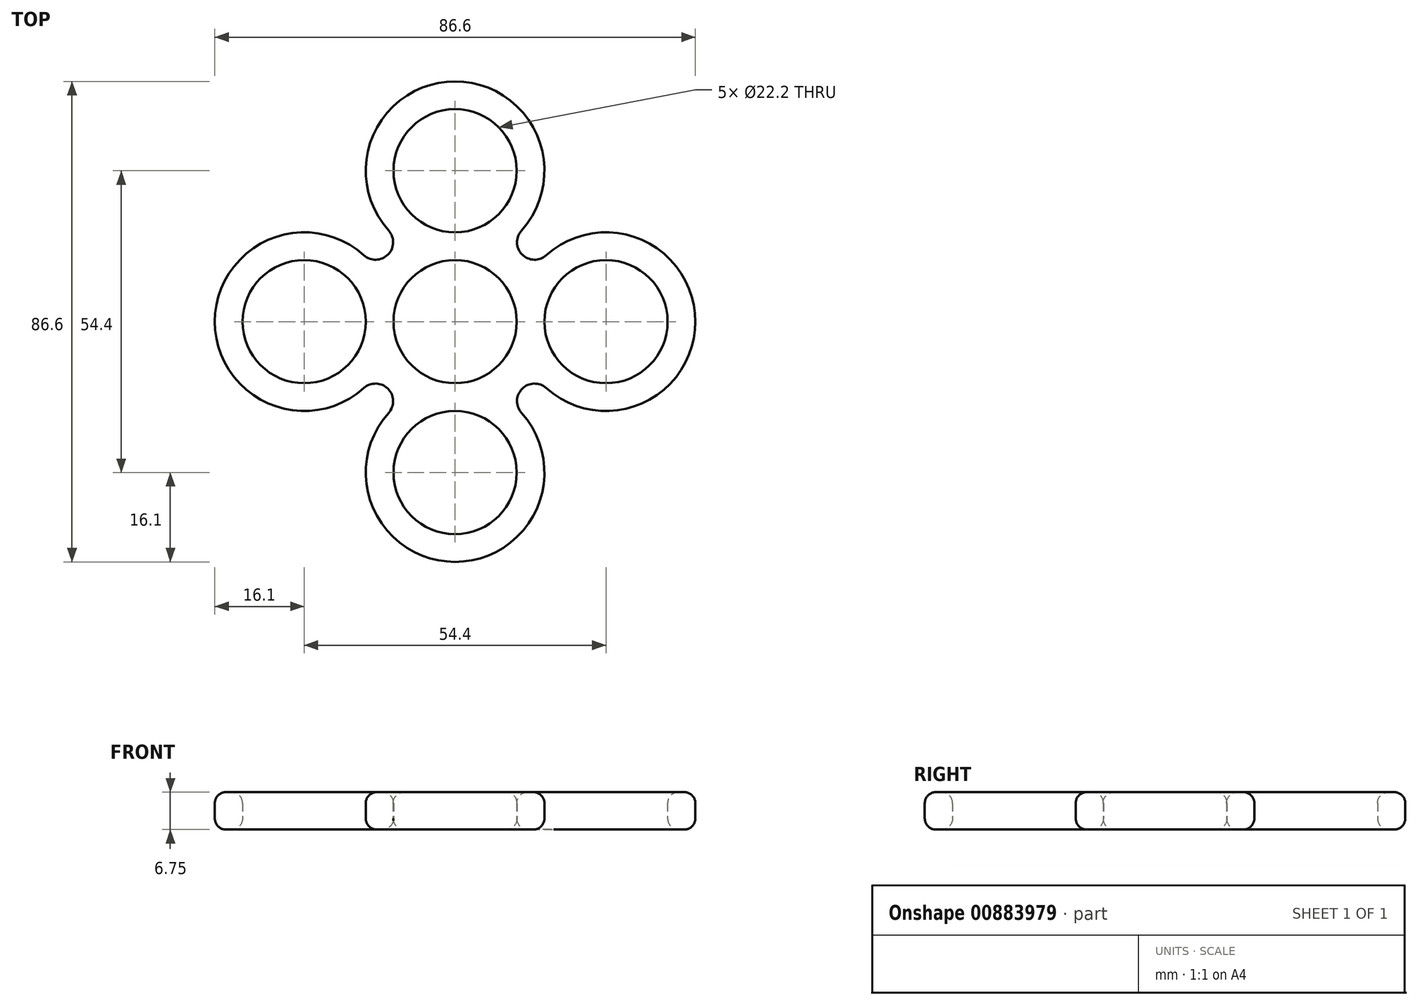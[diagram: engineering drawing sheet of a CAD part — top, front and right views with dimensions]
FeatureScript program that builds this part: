
annotation { "Feature Type Name" : "Feature", "Feature Type Description" : "" }
export const myFeature = defineFeature(function(context is Context, id is Id, definition is map)
    precondition{}
    {
        {
            var Q0;
            Q0=qCreatedBy(makeId("Top.planeOp"),FACE);
            var sketch = newSketch(context, id + "F0", { "sketchPlane" : qUnion([Q0])});
            skCircle(sketch, "E0", {"center": v(0, 0) * mm, "radius": 11.1 * mm});
            skCircle(sketch, "E1", {"center": v(0, 27.2) * mm, "radius": 11.1 * mm});
            skCircle(sketch, "E2.1.0", {"center": v(-27.2, 0) * mm, "radius": 11.1 * mm});
            skCircle(sketch, "E2.2.0", {"center": v(0, -27.2) * mm, "radius": 11.1 * mm});
            skCircle(sketch, "E2.3.0", {"center": v(27.2, 0) * mm, "radius": 11.1 * mm});
            skArc(sketch, "E3", {"start": v(-11.98, 16.44) * mm, "mid": v(0, 43.3) * mm, "end": v(11.98, 16.44) * mm});
            skArc(sketch, "E4.1.0", {"start": v(-16.44, -11.98) * mm, "mid": v(-43.3, 0) * mm, "end": v(-16.44, 11.98) * mm});
            skArc(sketch, "E4.2.0", {"start": v(11.98, -16.44) * mm, "mid": v(0, -43.3) * mm, "end": v(-11.98, -16.44) * mm});
            skArc(sketch, "E4.3.0", {"start": v(16.44, 11.98) * mm, "mid": v(43.3, 0) * mm, "end": v(16.44, -11.98) * mm});
            skArc(sketch, "E5", {"start": v(-11.98, 16.44) * mm, "mid": v(-12.1, 12.1) * mm, "end": v(-16.44, 11.98) * mm});
            skArc(sketch, "E6", {"start": v(-16.44, -11.98) * mm, "mid": v(-12.1, -12.1) * mm, "end": v(-11.98, -16.44) * mm});
            skArc(sketch, "E7", {"start": v(11.98, -16.44) * mm, "mid": v(12.1, -12.1) * mm, "end": v(16.44, -11.98) * mm});
            skArc(sketch, "E8", {"start": v(16.44, 11.98) * mm, "mid": v(12.1, 12.1) * mm, "end": v(11.98, 16.44) * mm});
            skSolve(sketch);
        }
        {
            var Q0;
            Q0=makeQuery(id+"F0.imprint","IMPRINT",FACE,{"disambiguationData":[TD([[makeQuery(id+"F0.imprint","IMPRINT",EDGE,{"derivedFrom":sQuery(id+"F0.wireOp",EDGE,"E0")}),-1.0]])]});
            extrude(context, id + "F1", {"entities" : qUnion([Q0]), "depth" : 6.75 * mm, "offsetDistance" : 25 * mm});
        }
        {
            var Q0;
            Q0=makeQuery(id+"F1.opExtrude","CAP_EDGE",EDGE,{"disambiguationData":[OSD([sQuery(id+"F0.wireOp",EDGE,"E1")])],"isStart":false});
            var Q1;
            Q1=makeQuery(id+"F1.opExtrude","CAP_EDGE",EDGE,{"disambiguationData":[OSD([sQuery(id+"F0.wireOp",EDGE,"E3")])],"isStart":false});
            var Q2;
            Q2=makeQuery(id+"F1.opExtrude","CAP_EDGE",EDGE,{"disambiguationData":[OSD([sQuery(id+"F0.wireOp",EDGE,"E0")])],"isStart":false});
            var Q3;
            Q3=makeQuery(id+"F1.opExtrude","CAP_EDGE",EDGE,{"disambiguationData":[OSD([sQuery(id+"F0.wireOp",EDGE,"E2.1.0")])],"isStart":false});
            var Q4;
            Q4=makeQuery(id+"F1.opExtrude","CAP_EDGE",EDGE,{"disambiguationData":[OSD([sQuery(id+"F0.wireOp",EDGE,"E2.2.0")])],"isStart":false});
            var Q5;
            Q5=makeQuery(id+"F1.opExtrude","CAP_EDGE",EDGE,{"disambiguationData":[OSD([sQuery(id+"F0.wireOp",EDGE,"E2.3.0")])],"isStart":false});
            var Q6;
            Q6=makeQuery(id+"F1.opExtrude","CAP_EDGE",EDGE,{"disambiguationData":[OSD([sQuery(id+"F0.wireOp",EDGE,"E2.3.0")])],"isStart":true});
            var Q7;
            Q7=makeQuery(id+"F1.opExtrude","CAP_EDGE",EDGE,{"disambiguationData":[OSD([sQuery(id+"F0.wireOp",EDGE,"E0")])],"isStart":true});
            var Q8;
            Q8=makeQuery(id+"F1.opExtrude","CAP_EDGE",EDGE,{"disambiguationData":[OSD([sQuery(id+"F0.wireOp",EDGE,"E2.2.0")])],"isStart":true});
            var Q9;
            Q9=makeQuery(id+"F1.opExtrude","CAP_EDGE",EDGE,{"disambiguationData":[OSD([sQuery(id+"F0.wireOp",EDGE,"E4.1.0")])],"isStart":true});
            var Q10;
            Q10=makeQuery(id+"F1.opExtrude","CAP_EDGE",EDGE,{"disambiguationData":[OSD([sQuery(id+"F0.wireOp",EDGE,"E2.1.0")])],"isStart":true});
            var Q11;
            Q11=makeQuery(id+"F1.opExtrude","CAP_EDGE",EDGE,{"disambiguationData":[OSD([sQuery(id+"F0.wireOp",EDGE,"E1")])],"isStart":true});
            fillet(context, id + "F2", {"entities" : qUnion([Q0, Q1, Q2, Q3, Q4, Q5, Q6, Q7, Q8, Q9, Q10, Q11]), "radius" : 2 * mm, "tangentPropagation" : true, "allowEdgeOverflow" : false});
        }
    });
